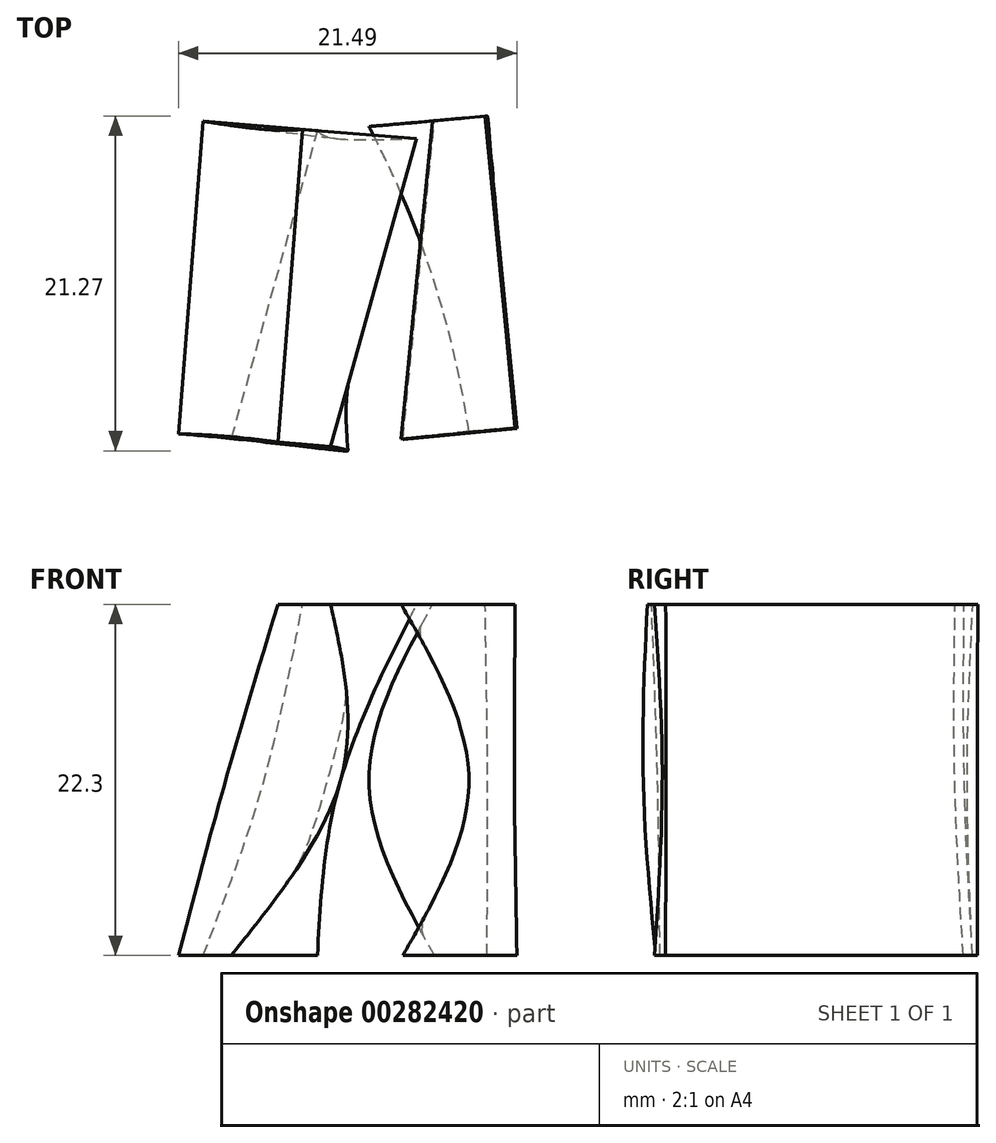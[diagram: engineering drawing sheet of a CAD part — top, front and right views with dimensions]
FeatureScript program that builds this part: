
annotation { "Feature Type Name" : "Feature", "Feature Type Description" : "" }
export const myFeature = defineFeature(function(context is Context, id is Id, definition is map)
    precondition{}
    {
        {
            var Q0;
            Q0=qCreatedBy(makeId("Top.planeOp"),FACE);
            cPlane(context, id + "F0", {"entities" : qUnion([Q0]), "cplaneType" : CPlaneType.OFFSET, "offset" : 11 * mm, "width" : 150 * mm, "height" : 150 * mm});
        }
        {
            var Q0;
            Q0=qCreatedBy(makeId("Top.planeOp"),FACE);
            cPlane(context, id + "F1", {"entities" : qUnion([Q0]), "cplaneType" : CPlaneType.OFFSET, "offset" : 22.3 * mm, "width" : 150 * mm, "height" : 150 * mm});
        }
        {
            var Q0;
            Q0=qCreatedBy(makeId("Top.planeOp"),FACE);
            var sketch = newSketch(context, id + "F2", { "sketchPlane" : qUnion([Q0])});
            skLineSegment(sketch, "E0.bottom", {"start": v(12, -12) * mm, "end": v(-12, -12) * mm, "construction": true});
            skLineSegment(sketch, "E0.top", {"start": v(12, 12) * mm, "end": v(-12, 12) * mm, "construction": true});
            skLineSegment(sketch, "E0.left", {"start": v(12, -12) * mm, "end": v(12, 12) * mm, "construction": true});
            skLineSegment(sketch, "E0.right", {"start": v(-12, -12) * mm, "end": v(-12, 12) * mm, "construction": true});
            skPoint(sketch, "E0.middle", {"position": v(0, 0) * mm});
            skPoint(sketch, "E1.middle", {"position": v(0.07, -0.98) * mm});
            skLineSegment(sketch, "E2", {"start": v(8.54, 10.4) * mm, "end": v(10.44, -9.41) * mm});
            skLineSegment(sketch, "E3", {"start": v(10.44, -9.41) * mm, "end": v(3.2, -10.1) * mm});
            skLineSegment(sketch, "E4", {"start": v(8.54, 10.4) * mm, "end": v(5.2, 10.09) * mm});
            skLineSegment(sketch, "E5", {"start": v(3.2, -10.1) * mm, "end": v(5.2, 10.09) * mm});
            skLineSegment(sketch, "E6", {"start": v(-11.05, -9.76) * mm, "end": v(-9.48, 10.1) * mm});
            skLineSegment(sketch, "E7", {"start": v(-9.48, 10.1) * mm, "end": v(-2.23, 9.52) * mm});
            skLineSegment(sketch, "E8", {"start": v(-11.05, -9.76) * mm, "end": v(-7.7, -10.02) * mm});
            skLineSegment(sketch, "E9", {"start": v(-2.23, 9.52) * mm, "end": v(-7.7, -10.02) * mm});
            skSolve(sketch);
        }
        {
            var Q0;
            Q0=qCreatedBy(id+"F1.planeOp",FACE);
            var sketch = newSketch(context, id + "F3", { "sketchPlane" : qUnion([Q0])});
            skLineSegment(sketch, "E10.bottom", {"start": v(11.9, -11.98) * mm, "end": v(-12.1, -11.98) * mm, "construction": true});
            skLineSegment(sketch, "E10.top", {"start": v(11.9, 12.02) * mm, "end": v(-12.1, 12.02) * mm, "construction": true});
            skLineSegment(sketch, "E10.left", {"start": v(11.9, -11.98) * mm, "end": v(11.9, 12.02) * mm, "construction": true});
            skLineSegment(sketch, "E10.right", {"start": v(-12.1, -11.98) * mm, "end": v(-12.1, 12.02) * mm, "construction": true});
            skPoint(sketch, "E10.middle", {"position": v(-0.1, 0.02) * mm});
            skPoint(sketch, "E11.middle", {"position": v(-0.04, -0.96) * mm});
            skLineSegment(sketch, "E12", {"start": v(8.43, 10.43) * mm, "end": v(10.33, -9.39) * mm});
            skLineSegment(sketch, "E13", {"start": v(10.33, -9.39) * mm, "end": v(3.09, -10.08) * mm});
            skLineSegment(sketch, "E14", {"start": v(8.43, 10.43) * mm, "end": v(5.09, 10.11) * mm});
            skLineSegment(sketch, "E15", {"start": v(3.09, -10.08) * mm, "end": v(5.09, 10.11) * mm});
            skLineSegment(sketch, "E16", {"start": v(-4.74, -10.29) * mm, "end": v(-3.17, 9.56) * mm});
            skLineSegment(sketch, "E17", {"start": v(-3.17, 9.56) * mm, "end": v(4.08, 9) * mm});
            skLineSegment(sketch, "E18", {"start": v(-4.74, -10.29) * mm, "end": v(-1.4, -10.55) * mm});
            skLineSegment(sketch, "E19", {"start": v(4.08, 9) * mm, "end": v(-1.4, -10.55) * mm});
            skSolve(sketch);
        }
        {
            var Q0;
            Q0=qCreatedBy(id+"F0.planeOp",FACE);
            var sketch = newSketch(context, id + "F4", { "sketchPlane" : qUnion([Q0])});
            skLineSegment(sketch, "E20", {"start": v(-5.65, 9.58) * mm, "end": v(-8.09, -9.9) * mm});
            skLineSegment(sketch, "E21", {"start": v(-8.09, -9.9) * mm, "end": v(-0.8, -10.81) * mm});
            skLineSegment(sketch, "E22", {"start": v(-5.65, 9.58) * mm, "end": v(-0.8, 8.98) * mm});
            skArc(sketch, "E23", {"start": v(-0.8, 8.98) * mm, "mid": v(-1.61, -0.92) * mm, "end": v(-0.8, -10.81) * mm});
            skLineSegment(sketch, "E24", {"start": v(10.29, -9.36) * mm, "end": v(8.58, 10.41) * mm});
            skLineSegment(sketch, "E25", {"start": v(8.58, 10.41) * mm, "end": v(1.05, 9.76) * mm});
            skLineSegment(sketch, "E26", {"start": v(10.29, -9.36) * mm, "end": v(7.4, -9.6) * mm});
            skArc(sketch, "E27", {"start": v(7.4, -9.6) * mm, "mid": v(5.05, 0.35) * mm, "end": v(1.05, 9.76) * mm});
            skSolve(sketch);
        }
        {
            var Q0;
            Q0=makeQuery(id+"F2.imprint","IMPRINT",FACE,{"disambiguationData":[TD([[makeQuery(id+"F2.imprint","IMPRINT",EDGE,{"derivedFrom":sQuery(id+"F2.wireOp",EDGE,"E6")}),-1.0]])]});
            var Q1;
            Q1=makeQuery(id+"F4.imprint","IMPRINT",FACE,{"disambiguationData":[TD([[makeQuery(id+"F4.imprint","IMPRINT",EDGE,{"derivedFrom":sQuery(id+"F4.wireOp",EDGE,"E20")}),1.0]])]});
            var Q2;
            Q2=makeQuery(id+"F3.imprint","IMPRINT",FACE,{"disambiguationData":[TD([[makeQuery(id+"F3.imprint","IMPRINT",EDGE,{"derivedFrom":sQuery(id+"F3.wireOp",EDGE,"E16")}),-1.0]])]});
            loft(context, id + "F5", {"sheetProfilesArray" : [{ "sheetProfileEntities" : qUnion([Q0]) }, { "sheetProfileEntities" : qUnion([Q1]) }, { "sheetProfileEntities" : qUnion([Q2]) }]});
        }
        {
            var Q0;
            Q0=makeQuery(id+"F2.imprint","IMPRINT",FACE,{"disambiguationData":[TD([[makeQuery(id+"F2.imprint","IMPRINT",EDGE,{"derivedFrom":sQuery(id+"F2.wireOp",EDGE,"E2")}),-1.0]])]});
            var Q1;
            Q1=makeQuery(id+"F4.imprint","IMPRINT",FACE,{"disambiguationData":[TD([[makeQuery(id+"F4.imprint","IMPRINT",EDGE,{"derivedFrom":sQuery(id+"F4.wireOp",EDGE,"E24")}),1.0]])]});
            var Q2;
            Q2=makeQuery(id+"F3.imprint","IMPRINT",FACE,{"disambiguationData":[TD([[makeQuery(id+"F3.imprint","IMPRINT",EDGE,{"derivedFrom":sQuery(id+"F3.wireOp",EDGE,"E12")}),-1.0]])]});
            loft(context, id + "F6", {"sheetProfilesArray" : [{ "sheetProfileEntities" : qUnion([Q0]) }, { "sheetProfileEntities" : qUnion([Q1]) }, { "sheetProfileEntities" : qUnion([Q2]) }]});
        }
    });
